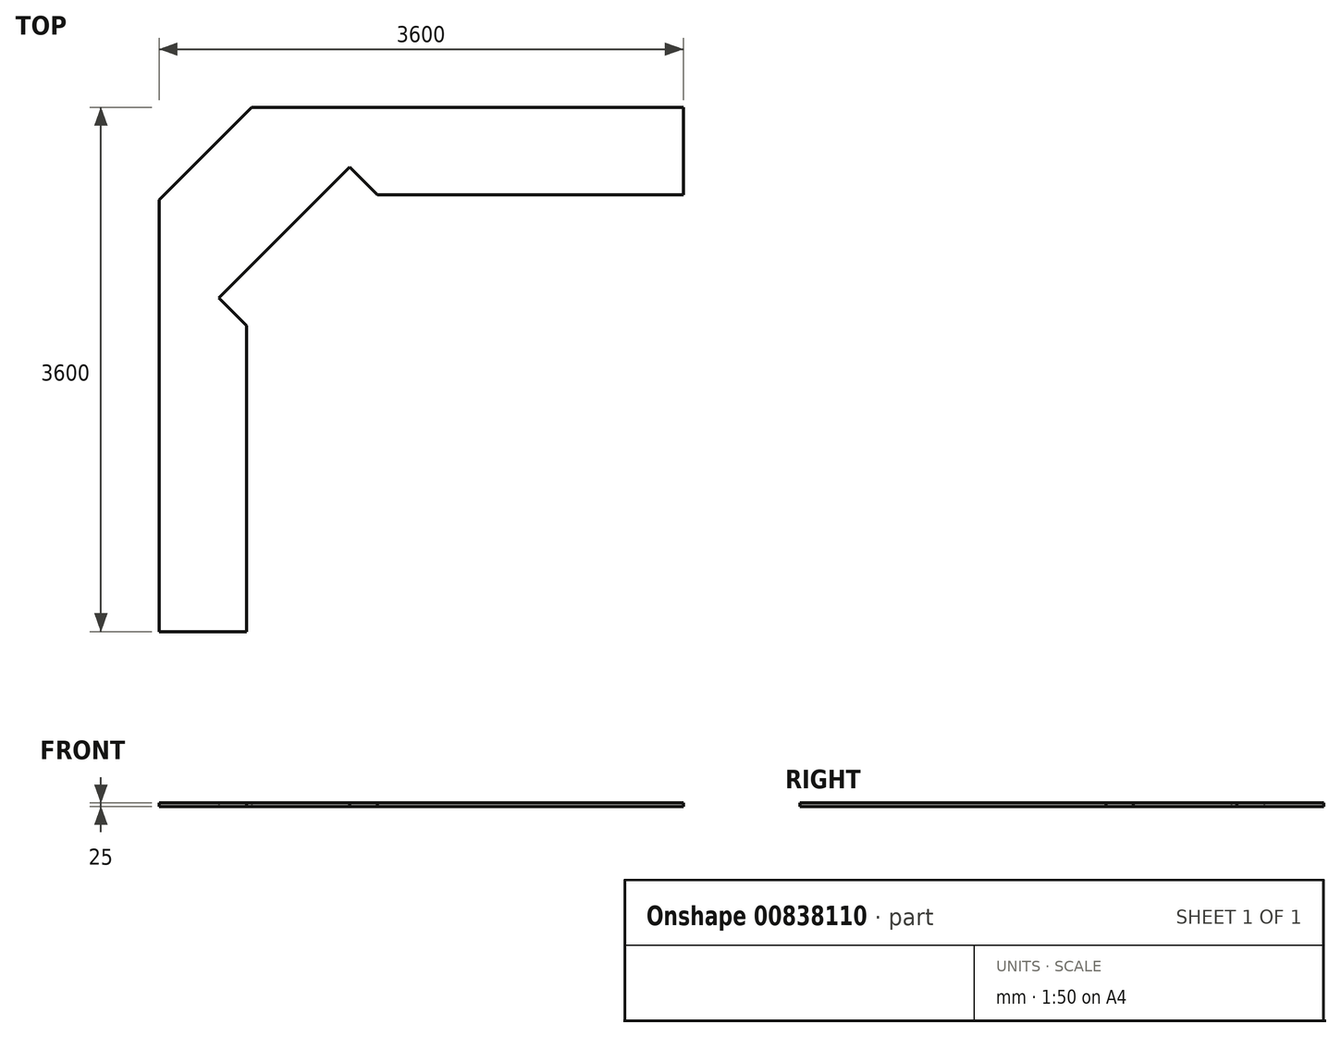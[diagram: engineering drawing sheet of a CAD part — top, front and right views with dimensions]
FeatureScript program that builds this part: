
annotation { "Feature Type Name" : "Feature", "Feature Type Description" : "" }
export const myFeature = defineFeature(function(context is Context, id is Id, definition is map)
    precondition{}
    {
        {
            var Q0;
            Q0=qCreatedBy(makeId("Top.planeOp"),FACE);
            var sketch = newSketch(context, id + "F0", { "sketchPlane" : qUnion([Q0])});
            skLineSegment(sketch, "E0", {"start": v(0, 0) * mm, "end": v(0, -3600) * mm});
            skLineSegment(sketch, "E1", {"start": v(0, 0) * mm, "end": v(3600, 0) * mm});
            skLineSegment(sketch, "E2", {"start": v(3600, 0) * mm, "end": v(0, -3600) * mm, "construction": true});
            skLineSegment(sketch, "E3", {"start": v(0, 0) * mm, "end": v(1800, -1800) * mm, "construction": true});
            skLineSegment(sketch, "E4", {"start": v(3600, 0) * mm, "end": v(3600, -600) * mm});
            skLineSegment(sketch, "E5", {"start": v(1498.03, -600) * mm, "end": v(1308.15, -410.12) * mm});
            skLineSegment(sketch, "E6", {"start": v(1308.15, -410.12) * mm, "end": v(410.12, -1308.15) * mm});
            skLineSegment(sketch, "E7", {"start": v(410.12, -1308.15) * mm, "end": v(600, -1498.03) * mm});
            skLineSegment(sketch, "E8", {"start": v(600, -1498.03) * mm, "end": v(600, -3600) * mm});
            skLineSegment(sketch, "E9", {"start": v(600, -3600) * mm, "end": v(0, -3600) * mm});
            skPoint(sketch, "E10", {"position": v(859.13, -859.13) * mm});
            skLineSegment(sketch, "E11", {"start": v(848.53, -190.92) * mm, "end": v(190.92, -848.53) * mm, "construction": true});
            skPoint(sketch, "E12", {"position": v(519.72, -519.72) * mm});
            skLineSegment(sketch, "E13", {"start": v(190.92, -848.53) * mm, "end": v(190.92, -1168.53) * mm, "construction": true});
            skLineSegment(sketch, "E14", {"start": v(848.53, -190.92) * mm, "end": v(1168.53, -190.92) * mm, "construction": true});
            skCircle(sketch, "E15", {"center": v(332.34, -332.34) * mm, "radius": 25 * mm, "construction": true});
            skLineSegment(sketch, "E16", {"start": v(332.34, -332.34) * mm, "end": v(-207.77, -872.45) * mm, "construction": true});
            skLineSegment(sketch, "E17", {"start": v(332.34, -332.34) * mm, "end": v(34.37, -976.79) * mm, "construction": true});
            skLineSegment(sketch, "E18", {"start": v(636.07, 0) * mm, "end": v(0, -636.07) * mm});
            skLineSegment(sketch, "E19", {"start": v(1308.15, -410.12) * mm, "end": v(1158.88, 0) * mm});
            skLineSegment(sketch, "E20", {"start": v(410.12, -1308.15) * mm, "end": v(0, -1158.88) * mm});
            skLineSegment(sketch, "E21", {"start": v(1498.03, -600) * mm, "end": v(1498.03, 0) * mm, "construction": true});
            skLineSegment(sketch, "E22", {"start": v(1998.03, -600) * mm, "end": v(1998.03, 0) * mm, "construction": true});
            skLineSegment(sketch, "E23", {"start": v(600, -1498.03) * mm, "end": v(0, -1498.03) * mm, "construction": true});
            skLineSegment(sketch, "E24", {"start": v(600, -2003.66) * mm, "end": v(0, -2003.66) * mm, "construction": true});
            skLineSegment(sketch, "E25.trimOffspring", {"start": v(2577.75, -600) * mm, "end": v(1498.03, -600) * mm});
            skLineSegment(sketch, "E26", {"start": v(2577.75, -600) * mm, "end": v(2577.75, 0) * mm, "construction": true});
            skLineSegment(sketch, "E27", {"start": v(2577.75, -600) * mm, "end": v(3600, -600) * mm});
            skSolve(sketch);
        }
        {
            var Q0;
            {var subQ5=sQuery(id+"F0.wireOp",EDGE,"E4");Q0=makeQuery(id+"F0.imprint","IMPRINT",FACE,{"disambiguationData":[TD([[makeQuery(id+"F0.imprint","IMPRINT",EDGE,{"derivedFrom":subQ5}),-1.0]])]});}
            var Q1;
            {var subQ0=sQuery(id+"F0.wireOp",EDGE,"E18");Q1=makeQuery(id+"F0.imprint","IMPRINT",FACE,{"disambiguationData":[TD([[makeQuery(id+"F0.imprint","IMPRINT",EDGE,{"derivedFrom":subQ0}),1.0]])]});}
            var Q2;
            {var subQ1=sQuery(id+"F0.wireOp",EDGE,"E7");Q2=makeQuery(id+"F0.imprint","IMPRINT",FACE,{"disambiguationData":[TD([[makeQuery(id+"F0.imprint","IMPRINT",EDGE,{"derivedFrom":subQ1}),-1.0]])]});}
            extrude(context, id + "F1", {"entities" : qUnion([Q0, Q1, Q2]), "depth" : 25 * mm, "offsetDistance" : 25 * mm});
        }
    });
